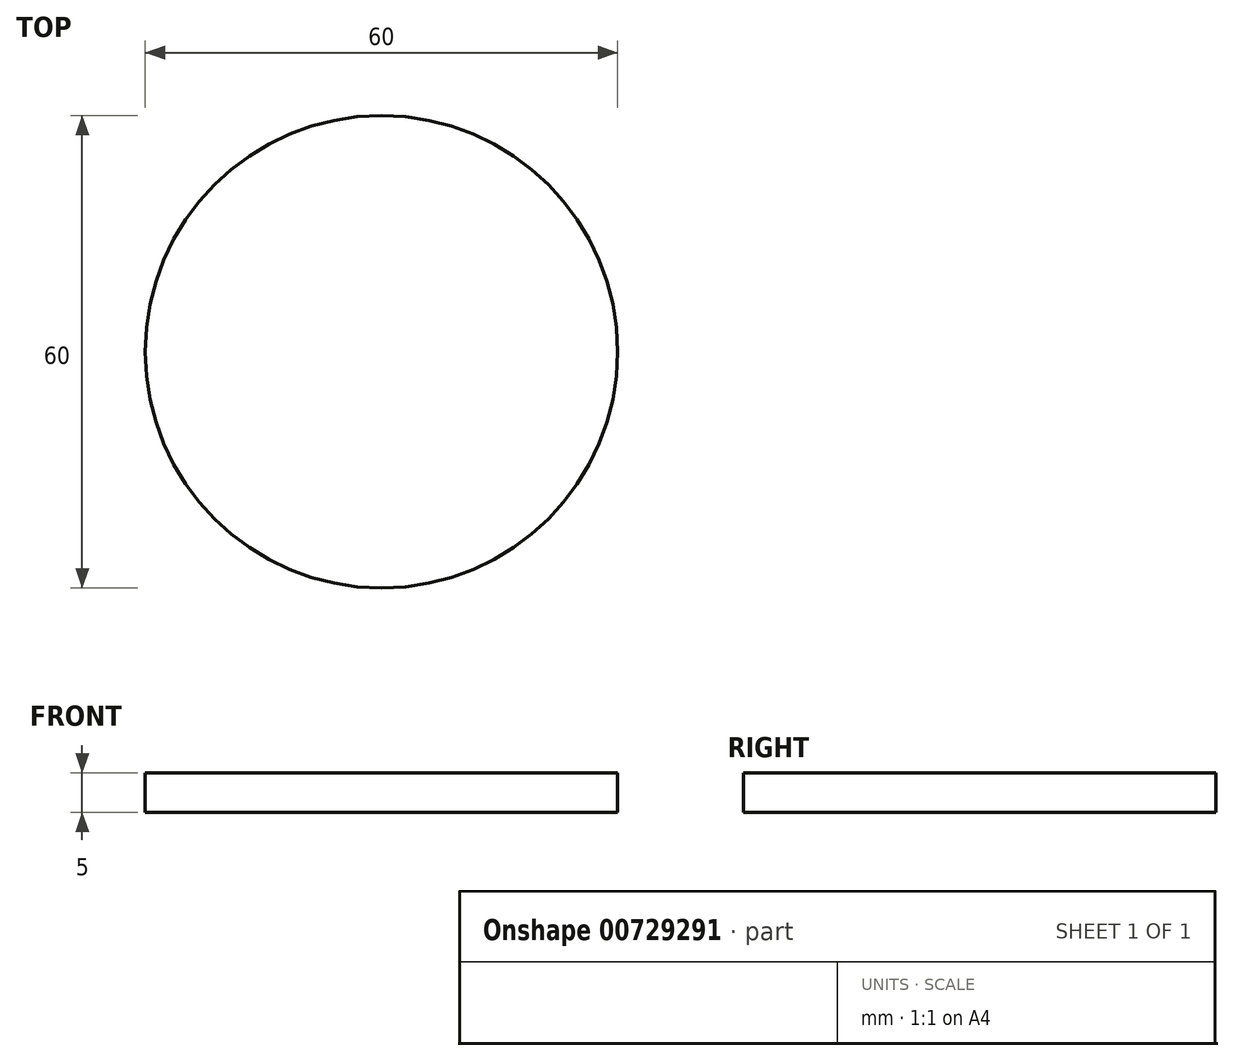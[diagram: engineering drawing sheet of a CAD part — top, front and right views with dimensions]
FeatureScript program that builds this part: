
annotation { "Feature Type Name" : "Feature", "Feature Type Description" : "" }
export const myFeature = defineFeature(function(context is Context, id is Id, definition is map)
    precondition{}
    {
        {
            var Q0;
            Q0=qCreatedBy(makeId("Top.planeOp"),FACE);
            var sketch = newSketch(context, id + "F0", { "sketchPlane" : qUnion([Q0])});
            skCircle(sketch, "E0", {"center": v(0, 0) * mm, "radius": 30 * mm});
            skSolve(sketch);
        }
        {
            var Q0;
            Q0 = qSketchRegion(id + "F0", true);
            extrude(context, id + "F1", {"entities" : qUnion([Q0]), "depth" : 5 * mm, "offsetDistance" : 25 * mm});
        }
    });
